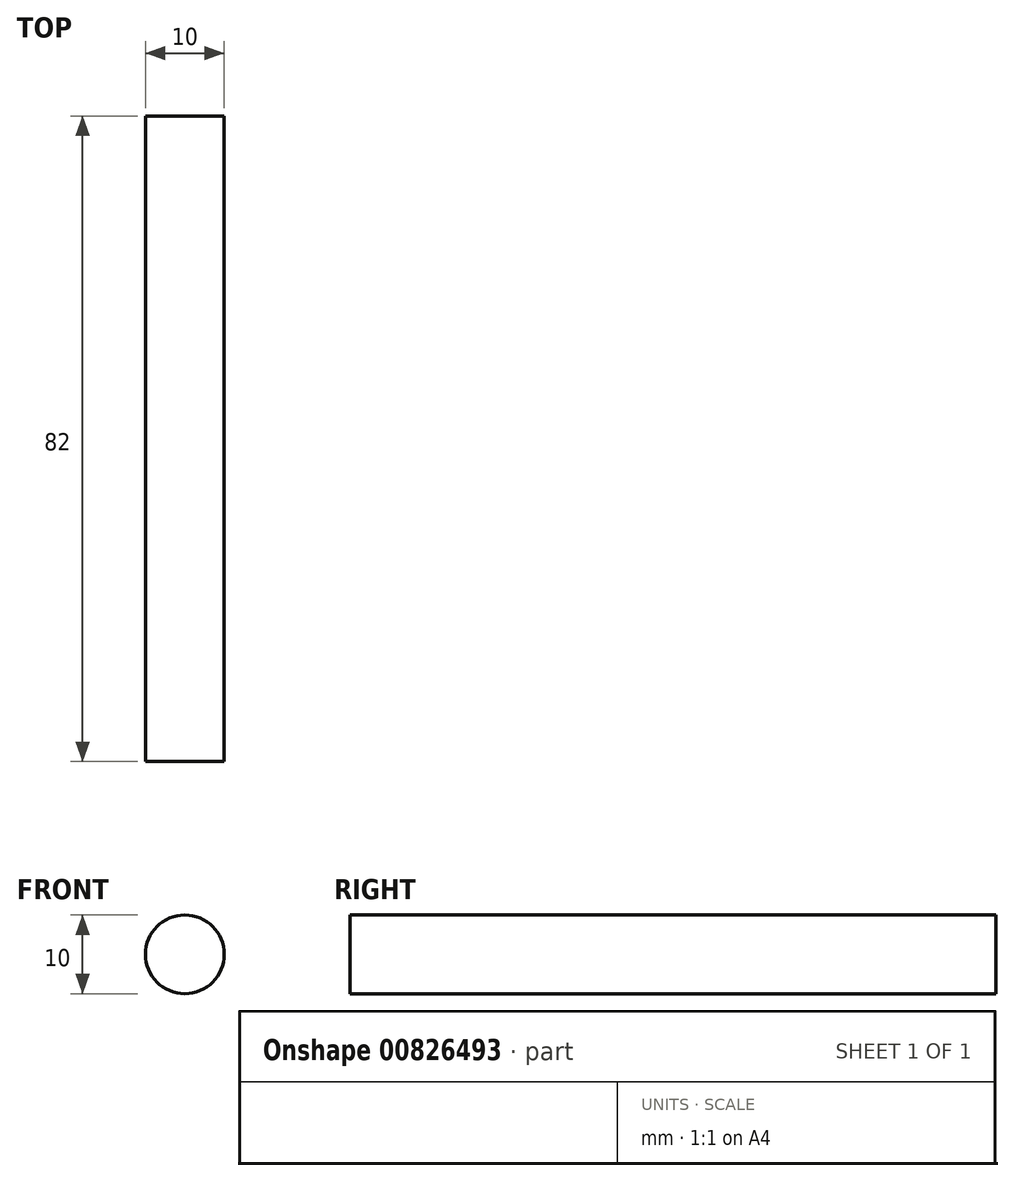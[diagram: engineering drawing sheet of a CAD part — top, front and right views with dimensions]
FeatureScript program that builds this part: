
annotation { "Feature Type Name" : "Feature", "Feature Type Description" : "" }
export const myFeature = defineFeature(function(context is Context, id is Id, definition is map)
    precondition{}
    {
        {
            var Q0;
            Q0=qCreatedBy(makeId("Front.planeOp"),FACE);
            var sketch = newSketch(context, id + "F0", { "sketchPlane" : qUnion([Q0])});
            skCircle(sketch, "E0", {"center": v(0, 0) * mm, "radius": 5 * mm});
            skSolve(sketch);
        }
        {
            var Q0;
            Q0 = qSketchRegion(id + "F0", true);
            extrude(context, id + "F1", {"entities" : qUnion([Q0]), "depth" : 82 * mm, "offsetDistance" : 25 * mm});
        }
    });
